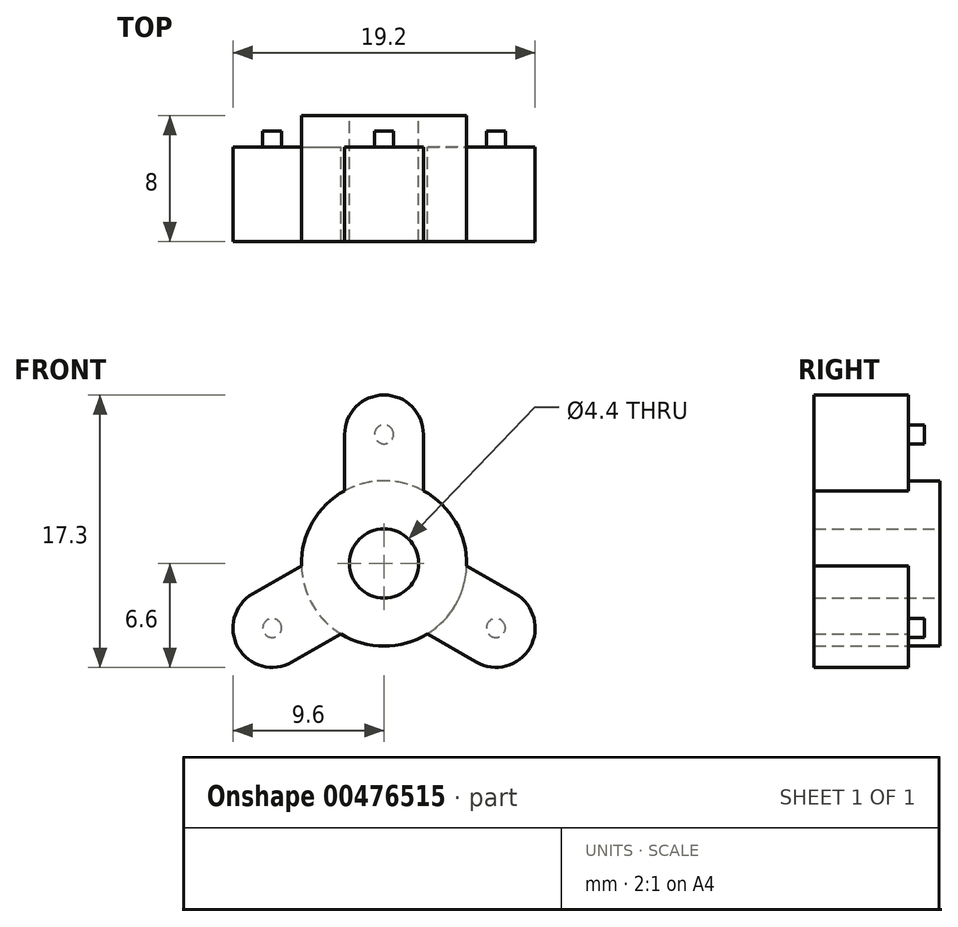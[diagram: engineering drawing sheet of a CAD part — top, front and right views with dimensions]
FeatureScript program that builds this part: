
annotation { "Feature Type Name" : "Feature", "Feature Type Description" : "" }
export const myFeature = defineFeature(function(context is Context, id is Id, definition is map)
    precondition{}
    {
        {
            var Q0;
            Q0=qCreatedBy(makeId("Front.planeOp"),FACE);
            var sketch = newSketch(context, id + "F0", { "sketchPlane" : qUnion([Q0])});
            skCircle(sketch, "E0", {"center": v(0, 0) * mm, "radius": 8.2 * mm, "construction": true});
            skCircle(sketch, "E1", {"center": v(0, 8.2) * mm, "radius": 0.6 * mm});
            skArc(sketch, "E2", {"start": v(2.47, 7.82) * mm, "mid": v(0, 10.7) * mm, "end": v(-2.47, 7.82) * mm});
            skArc(sketch, "E3", {"start": v(-2.5, 4.62) * mm, "mid": v(-4.55, 2.63) * mm, "end": v(-5.25, -0.14) * mm});
            skLineSegment(sketch, "E4", {"start": v(2.5, 8.2) * mm, "end": v(2.5, 4.62) * mm});
            skLineSegment(sketch, "E5", {"start": v(-2.5, 8.2) * mm, "end": v(-2.5, 4.62) * mm});
            skLineSegment(sketch, "E6", {"start": v(-2.5, 4.62) * mm, "end": v(2.5, 4.62) * mm, "construction": true});
            skLineSegment(sketch, "E7.1.0", {"start": v(-5.85, -6.27) * mm, "end": v(-2.75, -4.47) * mm});
            skArc(sketch, "E7.1.1", {"start": v(-8, -1.77) * mm, "mid": v(-9.27, -5.35) * mm, "end": v(-5.54, -6.05) * mm});
            skCircle(sketch, "E7.1.2", {"center": v(-7.1, -4.1) * mm, "radius": 0.6 * mm});
            skLineSegment(sketch, "E7.1.3", {"start": v(-8.35, -1.93) * mm, "end": v(-5.25, -0.14) * mm});
            skLineSegment(sketch, "E7.1.4", {"start": v(-2.75, -4.47) * mm, "end": v(-5.25, -0.14) * mm, "construction": true});
            skLineSegment(sketch, "E7.2.0", {"start": v(8.35, -1.93) * mm, "end": v(5.25, -0.14) * mm});
            skArc(sketch, "E7.2.1", {"start": v(5.54, -6.05) * mm, "mid": v(9.27, -5.35) * mm, "end": v(8, -1.77) * mm});
            skCircle(sketch, "E7.2.2", {"center": v(7.1, -4.1) * mm, "radius": 0.6 * mm});
            skLineSegment(sketch, "E7.2.3", {"start": v(5.85, -6.27) * mm, "end": v(2.75, -4.47) * mm});
            skLineSegment(sketch, "E7.2.4", {"start": v(5.25, -0.14) * mm, "end": v(2.75, -4.47) * mm, "construction": true});
            skLineSegment(sketch, "E8", {"start": v(-2.5, 4.62) * mm, "end": v(-5.25, -0.14) * mm, "construction": true});
            skLineSegment(sketch, "E9", {"start": v(-2.75, -4.47) * mm, "end": v(2.75, -4.47) * mm, "construction": true});
            skLineSegment(sketch, "E10", {"start": v(5.25, -0.14) * mm, "end": v(2.5, 4.62) * mm, "construction": true});
            skArc(sketch, "E11.trimOffspring", {"start": v(-2.75, -4.47) * mm, "mid": v(0, -5.25) * mm, "end": v(2.75, -4.47) * mm});
            skArc(sketch, "E12.trimOffspring", {"start": v(5.25, -0.14) * mm, "mid": v(4.55, 2.63) * mm, "end": v(2.5, 4.62) * mm});
            skSolve(sketch);
        }
        {
            var Q0;
            Q0=makeQuery(id+"F0.imprint","IMPRINT",FACE,{"disambiguationData":[TD([[makeQuery(id+"F0.imprint","IMPRINT",EDGE,{"derivedFrom":sQuery(id+"F0.wireOp",EDGE,"E1")}),-1.0]])]});
            var Q1;
            Q1=makeQuery(id+"F0.imprint","IMPRINT",FACE,{"disambiguationData":[TD([[makeQuery(id+"F0.imprint","IMPRINT",EDGE,{"derivedFrom":sQuery(id+"F0.wireOp",EDGE,"E7.2.2")}),1.0]])]});
            var Q2;
            Q2=makeQuery(id+"F0.imprint","IMPRINT",FACE,{"disambiguationData":[TD([[makeQuery(id+"F0.imprint","IMPRINT",EDGE,{"derivedFrom":sQuery(id+"F0.wireOp",EDGE,"E1")}),1.0]])]});
            var Q3;
            Q3=makeQuery(id+"F0.imprint","IMPRINT",FACE,{"disambiguationData":[TD([[makeQuery(id+"F0.imprint","IMPRINT",EDGE,{"derivedFrom":sQuery(id+"F0.wireOp",EDGE,"E7.1.2")}),1.0]])]});
            extrude(context, id + "F1", {"entities" : qUnion([Q0, Q1, Q2, Q3]), "depth" : 6 * mm});
        }
        {
            var Q0;
            Q0=makeQuery(id+"F0.imprint","IMPRINT",FACE,{"disambiguationData":[TD([[makeQuery(id+"F0.imprint","IMPRINT",EDGE,{"derivedFrom":sQuery(id+"F0.wireOp",EDGE,"E7.1.2")}),1.0]])]});
            var Q1;
            Q1=makeQuery(id+"F0.imprint","IMPRINT",FACE,{"disambiguationData":[TD([[makeQuery(id+"F0.imprint","IMPRINT",EDGE,{"derivedFrom":sQuery(id+"F0.wireOp",EDGE,"E7.2.2")}),1.0]])]});
            var Q2;
            Q2=makeQuery(id+"F0.imprint","IMPRINT",FACE,{"disambiguationData":[TD([[makeQuery(id+"F0.imprint","IMPRINT",EDGE,{"derivedFrom":sQuery(id+"F0.wireOp",EDGE,"E1")}),1.0]])]});
            extrude(context, id + "F2", {"entities" : qUnion([Q0, Q1, Q2]), "operationType" : NewBodyOperationType.ADD, "oppositeDirection" : true, "depth" : 1 * mm});
        }
        {
            var Q0;
            Q0=makeQuery(id+"F0.imprint","IMPRINT",FACE,{"disambiguationData":[TD([[makeQuery(id+"F0.imprint","IMPRINT",EDGE,{"derivedFrom":sQuery(id+"F0.wireOp",EDGE,"E1")}),-1.0]])]});
            var sketch = newSketch(context, id + "F3", { "sketchPlane" : qUnion([Q0])});
            skPoint(sketch, "E13.0", {"position": v(0, 0) * mm});
            skPoint(sketch, "E14.0", {"position": v(2.75, -4.47) * mm});
            skCircle(sketch, "E15", {"center": v(0, 0) * mm, "radius": 5.25 * mm});
            skSolve(sketch);
        }
        {
            var Q0;
            {var subQ0=sQuery(id+"F3.wireOp",EDGE,"E15");var subQ1=makeQuery(id+"F3.imprint","INTERSECT",VERTEX,{"derivedFrom":[makeQuery(id+"F0.imprint","IMPRINT",EDGE,{"derivedFrom":sQuery(id+"F0.wireOp",EDGE,"E5")}),subQ0]});Q0=makeQuery(id+"F3.imprint","IMPRINT",FACE,{"disambiguationData":[TD([[makeQuery(id+"F3.imprint","IMPRINT",EDGE,{"disambiguationData":[TD([[subQ1,-1.0]])],"derivedFrom":subQ0}),1.0]])]});}
            var Q1;
            Q1=sQuery(id+"F3.wireOp",EDGE,"E15");
            extrude(context, id + "F4", {"entities" : qUnion([Q0]), "operationType" : NewBodyOperationType.ADD, "surfaceEntities" : qUnion([Q1]), "oppositeDirection" : true, "depth" : 2 * mm});
        }
        {
            var Q0;
            Q0=sQuery(id+"F0.wireOp",VERTEX,"E0.center");
            var Q1;
            Q1=makeQuery(id+"F1.opExtrude","SWEPT_BODY",BODY,{"disambiguationData":[OSD([sQuery(id+"F0.wireOp",EDGE,"E2"),sQuery(id+"F0.wireOp",EDGE,"E3"),sQuery(id+"F0.wireOp",EDGE,"E4"),sQuery(id+"F0.wireOp",EDGE,"E5"),sQuery(id+"F0.wireOp",EDGE,"E7.1.0"),sQuery(id+"F0.wireOp",EDGE,"E7.1.1"),sQuery(id+"F0.wireOp",EDGE,"E7.1.3"),sQuery(id+"F0.wireOp",EDGE,"E7.2.0"),sQuery(id+"F0.wireOp",EDGE,"E7.2.1"),sQuery(id+"F0.wireOp",EDGE,"E7.2.3"),sQuery(id+"F0.wireOp",EDGE,"E11.trimOffspring"),sQuery(id+"F0.wireOp",EDGE,"E12.trimOffspring")])]});
            hole(context, id + "F5", {"style" : HoleStyle.SIMPLE, "endStyle" : HoleEndStyle.THROUGH, "oppositeDirection" : true, "standardTappedOrClearance" : lookupTablePath({ "standard" : "ISO", "fit" : "Normal", "size" : "M4", "type" : "Clearance" }), "standardBlindInLast" : lookupTablePath({ "fit" : "Standard", "standard" : "ISO", "size" : "M4", "type" : "Clearance" }), "holeDiameter" : 4.4 * mm, "tappedDepth" : 13.9 * mm, "tapClearance" : 3, "startFromSketch" : true, "locations" : qUnion([Q0]), "scope" : qUnion([Q1])});
        }
        {
            var Q0;
            Q0=sQuery(id+"F0.wireOp",VERTEX,"E0.center");
            var Q1;
            Q1=makeQuery(id+"F1.opExtrude","SWEPT_BODY",BODY,{"disambiguationData":[OSD([sQuery(id+"F0.wireOp",EDGE,"E2"),sQuery(id+"F0.wireOp",EDGE,"E3"),sQuery(id+"F0.wireOp",EDGE,"E4"),sQuery(id+"F0.wireOp",EDGE,"E5"),sQuery(id+"F0.wireOp",EDGE,"E7.1.0"),sQuery(id+"F0.wireOp",EDGE,"E7.1.1"),sQuery(id+"F0.wireOp",EDGE,"E7.1.3"),sQuery(id+"F0.wireOp",EDGE,"E7.2.0"),sQuery(id+"F0.wireOp",EDGE,"E7.2.1"),sQuery(id+"F0.wireOp",EDGE,"E7.2.3"),sQuery(id+"F0.wireOp",EDGE,"E11.trimOffspring"),sQuery(id+"F0.wireOp",EDGE,"E12.trimOffspring")])]});
            hole(context, id + "F6", {"style" : HoleStyle.SIMPLE, "endStyle" : HoleEndStyle.THROUGH, "standardTappedOrClearance" : lookupTablePath({ "standard" : "ISO", "fit" : "Normal", "size" : "M4", "type" : "Clearance" }), "standardBlindInLast" : lookupTablePath({ "fit" : "Standard", "standard" : "ISO", "size" : "M4", "type" : "Clearance" }), "holeDiameter" : 4.4 * mm, "tappedDepth" : 13.9 * mm, "tapClearance" : 3, "startFromSketch" : true, "locations" : qUnion([Q0]), "scope" : qUnion([Q1])});
        }
    });
